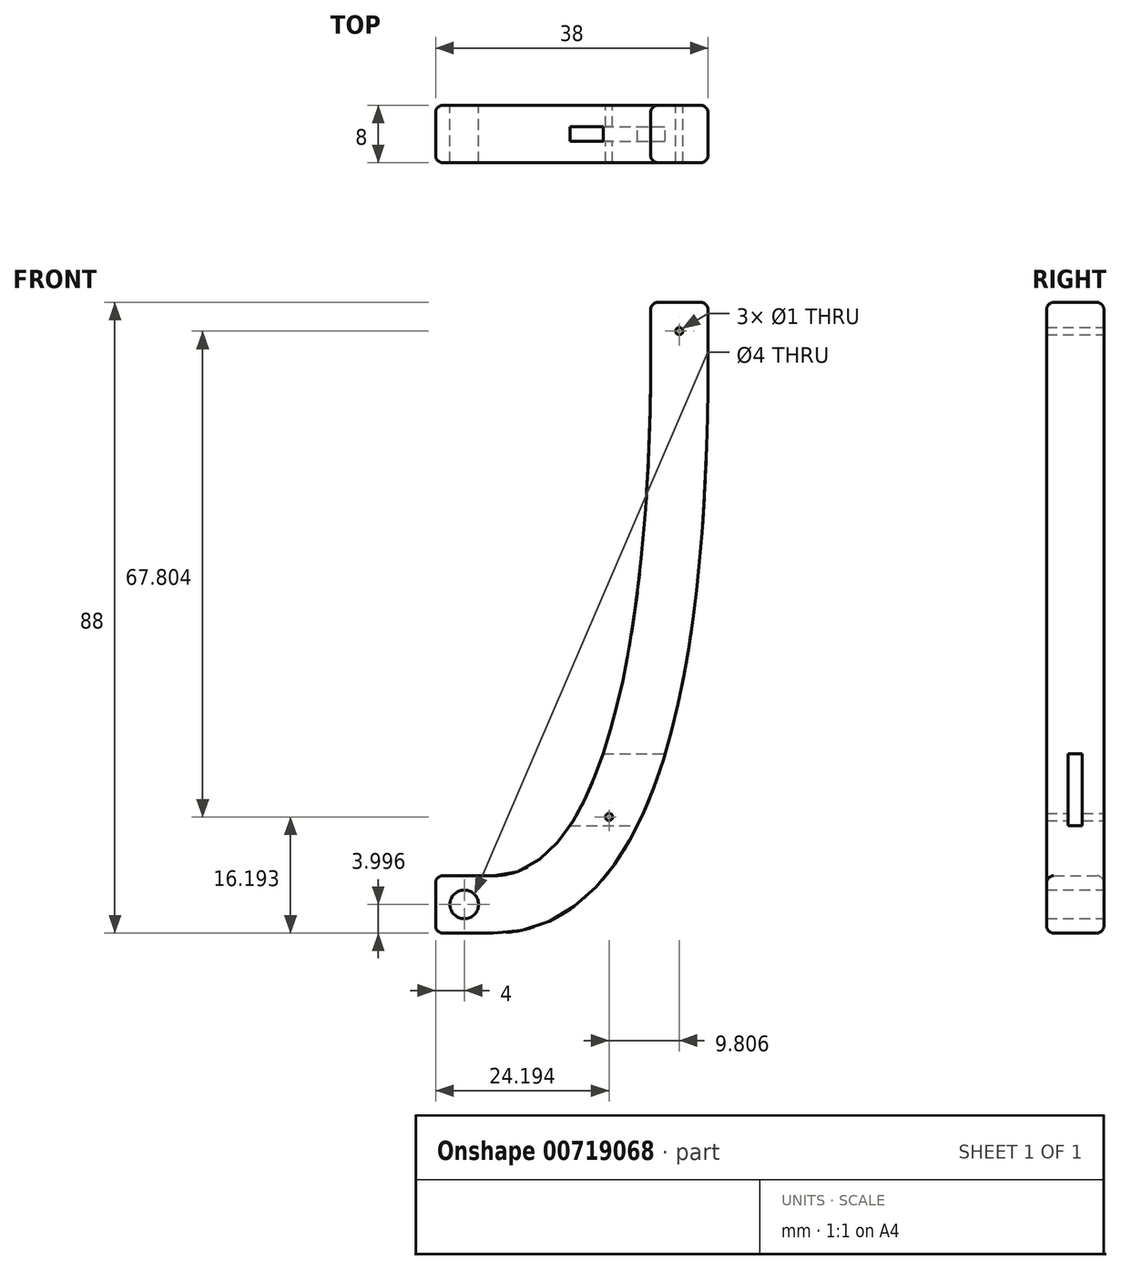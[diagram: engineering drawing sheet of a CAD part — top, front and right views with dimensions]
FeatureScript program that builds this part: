
annotation { "Feature Type Name" : "Feature", "Feature Type Description" : "" }
export const myFeature = defineFeature(function(context is Context, id is Id, definition is map)
    precondition{}
    {
        {
            var Q0;
            Q0=qCreatedBy(makeId("Front.planeOp"),FACE);
            var sketch = newSketch(context, id + "F0", { "sketchPlane" : qUnion([Q0])});
            skLineSegment(sketch, "E0.bottom", {"start": v(-30, -15.92) * mm, "end": v(-22, -15.92) * mm});
            skLineSegment(sketch, "E0.top", {"start": v(-30, -23.92) * mm, "end": v(-22, -23.92) * mm});
            skLineSegment(sketch, "E0.left", {"start": v(-30, -15.92) * mm, "end": v(-30, -23.92) * mm});
            skCircle(sketch, "E1", {"center": v(-26, -19.92) * mm, "radius": 2 * mm});
            skPoint(sketch, "E1.centerSnap0", {"position": v(-30, -19.92) * mm});
            skPoint(sketch, "E1.centerSnap1", {"position": v(-26, -15.92) * mm});
            skLineSegment(sketch, "E2.bottom", {"start": v(0, 64.08) * mm, "end": v(8, 64.08) * mm});
            skLineSegment(sketch, "E2.left", {"start": v(0, 64.08) * mm, "end": v(0, 56.08) * mm});
            skLineSegment(sketch, "E2.right", {"start": v(8, 64.08) * mm, "end": v(8, 56.08) * mm});
            skCircle(sketch, "E3", {"center": v(4, 60.08) * mm, "radius": 0.5 * mm});
            skPoint(sketch, "E3.centerSnap0", {"position": v(8, 60.08) * mm});
            skPoint(sketch, "E3.centerSnap1", {"position": v(4, 64.08) * mm});
            skFitSpline(sketch, "E4", {"points": [v(-22, -15.92) * mm, v(0, 56.08) * mm], "startDerivative": vector(48, 0) * mm, "endDerivative": vector(0, 108) * mm});
            skLineSegment(sketch, "E5", {"start": v(0, 56.08) * mm, "end": v(0, -40.46) * mm, "construction": true});
            skLineSegment(sketch, "E6", {"start": v(-22, -15.92) * mm, "end": v(23.34, -15.92) * mm, "construction": true});
            skLineSegment(sketch, "E7", {"start": v(-22, -23.92) * mm, "end": v(42.36, -23.92) * mm, "construction": true});
            skLineSegment(sketch, "E8", {"start": v(8, 56.08) * mm, "end": v(8, -42.95) * mm, "construction": true});
            skFitSpline(sketch, "E9", {"points": [v(-22, -23.92) * mm, v(8, 56.08) * mm], "startDerivative": vector(55.5, 0) * mm, "endDerivative": vector(0, 168) * mm});
            skPoint(sketch, "E10", {"position": v(8, 6.56) * mm});
            skCircle(sketch, "E11", {"center": v(-5.8, -7.73) * mm, "radius": 0.5 * mm});
            skSolve(sketch);
        }
        {
            var Q0;
            Q0 = qSketchRegion(id + "F0", true);
            extrude(context, id + "F1", {"entities" : qUnion([Q0]), "depth" : 8 * mm, "offsetDistance" : 25 * mm});
        }
        {
            var Q0;
            Q0=makeQuery(id+"F1.opExtrude","CAP_EDGE",EDGE,{"disambiguationData":[OSD([sQuery(id+"F0.wireOp",EDGE,"E9")])],"isStart":false});
            var Q1;
            Q1=makeQuery(id+"F1.opExtrude","CAP_EDGE",EDGE,{"disambiguationData":[OSD([sQuery(id+"F0.wireOp",EDGE,"E9")])],"isStart":true});
            var Q2;
            Q2=makeQuery(id+"F1.opExtrude","CAP_EDGE",EDGE,{"disambiguationData":[OSD([sQuery(id+"F0.wireOp",EDGE,"E4")])],"isStart":false});
            var Q3;
            Q3=makeQuery(id+"F1.opExtrude","CAP_EDGE",EDGE,{"disambiguationData":[OSD([sQuery(id+"F0.wireOp",EDGE,"E4")])],"isStart":true});
            var Q4;
            Q4=makeQuery(id+"F1.opExtrude","CAP_EDGE",EDGE,{"disambiguationData":[OSD([sQuery(id+"F0.wireOp",EDGE,"E2.left")])],"isStart":true});
            var Q5;
            Q5=makeQuery(id+"F1.opExtrude","CAP_EDGE",EDGE,{"disambiguationData":[OSD([sQuery(id+"F0.wireOp",EDGE,"E2.bottom")])],"isStart":true});
            var Q6;
            Q6=makeQuery(id+"F1.opExtrude","SWEPT_FACE",FACE,{"disambiguationData":[OSD([sQuery(id+"F0.wireOp",EDGE,"E2.bottom")])]});
            var Q7;
            Q7=makeQuery(id+"F1.opExtrude","SWEPT_FACE",FACE,{"disambiguationData":[OSD([sQuery(id+"F0.wireOp",EDGE,"E0.left")])]});
            fillet(context, id + "F2", {"entities" : qUnion([Q0, Q1, Q2, Q3, Q4, Q5, Q6, Q7]), "radius" : 1 * mm, "tangentPropagation" : true, "allowEdgeOverflow" : false});
        }
        {
            var Q0;
            Q0=makeQuery(id+"F1.opExtrude","SWEPT_FACE",FACE,{"disambiguationData":[OSD([sQuery(id+"F0.wireOp",EDGE,"E2.left")])]});
            var sketch = newSketch(context, id + "F3", { "sketchPlane" : qUnion([Q0])});
            skLineSegment(sketch, "E12.bottom", {"start": v(3, 1.08) * mm, "end": v(5, 1.08) * mm});
            skLineSegment(sketch, "E12.top", {"start": v(3, -8.92) * mm, "end": v(5, -8.92) * mm});
            skLineSegment(sketch, "E12.left", {"start": v(3, 1.08) * mm, "end": v(3, -8.92) * mm});
            skLineSegment(sketch, "E12.right", {"start": v(5, 1.08) * mm, "end": v(5, -8.92) * mm});
            skSolve(sketch);
        }
        {
            var Q0;
            Q0=makeQuery(id+"F3.imprint","IMPRINT",FACE,{"disambiguationData":[TD([[makeQuery(id+"F3.imprint","IMPRINT",EDGE,{"derivedFrom":sQuery(id+"F3.wireOp",EDGE,"E12.bottom")}),-1.0]])]});
            extrude(context, id + "F4", {"entities" : qUnion([Q0]), "operationType" : NewBodyOperationType.REMOVE, "endBound" : BoundingType.SYMMETRIC, "depth" : 50 * mm, "offsetDistance" : 25 * mm});
        }
    });
